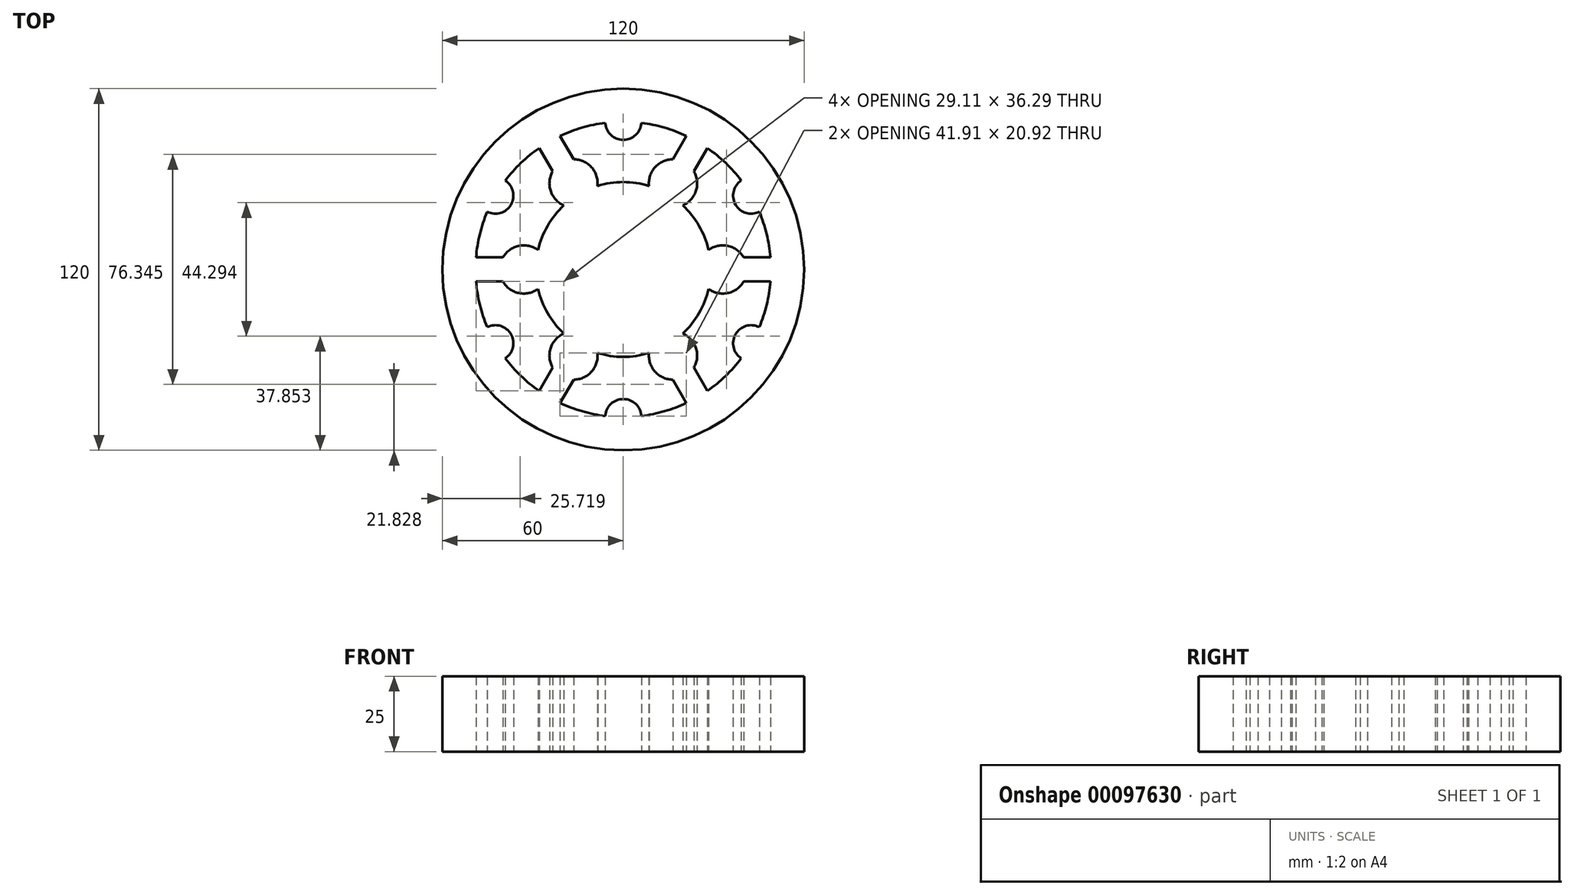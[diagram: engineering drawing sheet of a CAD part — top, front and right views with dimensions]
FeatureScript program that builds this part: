
annotation { "Feature Type Name" : "Feature", "Feature Type Description" : "" }
export const myFeature = defineFeature(function(context is Context, id is Id, definition is map)
    precondition{}
    {
        {
            var Q0;
            Q0=qCreatedBy(makeId("Top.planeOp"),FACE);
            var sketch = newSketch(context, id + "F0", { "sketchPlane" : qUnion([Q0])});
            skArc(sketch, "E0", {"start": v(-45.11, 19.13) * mm, "mid": v(-47.58, 11.71) * mm, "end": v(-48.84, 4) * mm});
            skCircle(sketch, "E1", {"center": v(0, 0) * mm, "radius": 33 * mm, "construction": true});
            skLineSegment(sketch, "E2", {"start": v(0, 0) * mm, "end": v(-49, 0) * mm, "construction": true});
            skLineSegment(sketch, "E3", {"start": v(0, 0) * mm, "end": v(-24.5, 42.44) * mm, "construction": true});
            skArc(sketch, "E4", {"start": v(-28.27, 6.45) * mm, "mid": v(-34.65, 7.83) * mm, "end": v(-39.93, 4) * mm});
            skArc(sketch, "E5", {"start": v(-23.43, 32.58) * mm, "mid": v(-24.1, 26.1) * mm, "end": v(-19.73, 21.26) * mm});
            skLineSegment(sketch, "E6", {"start": v(0, 0) * mm, "end": v(-42.44, 24.5) * mm, "construction": true});
            skArc(sketch, "E7", {"start": v(-45.11, 19.13) * mm, "mid": v(-37.24, 21.5) * mm, "end": v(-39.12, 29.5) * mm});
            skLineSegment(sketch, "E8", {"start": v(-27.88, 40.3) * mm, "end": v(-23.43, 32.58) * mm});
            skLineSegment(sketch, "E9", {"start": v(-48.84, 4) * mm, "end": v(-39.93, 4) * mm});
            skArc(sketch, "E10", {"start": v(-19.73, 21.26) * mm, "mid": v(-25.11, 14.5) * mm, "end": v(-28.27, 6.45) * mm});
            skArc(sketch, "E11.trimOffspring", {"start": v(-27.88, 40.3) * mm, "mid": v(-33.93, 35.35) * mm, "end": v(-39.12, 29.5) * mm});
            skArc(sketch, "E12.1.0", {"start": v(-39.12, -29.5) * mm, "mid": v(-33.93, -35.35) * mm, "end": v(-27.88, -40.3) * mm});
            skArc(sketch, "E12.1.1", {"start": v(-39.12, -29.5) * mm, "mid": v(-37.24, -21.5) * mm, "end": v(-45.11, -19.13) * mm});
            skArc(sketch, "E12.1.2", {"start": v(-48.84, -4) * mm, "mid": v(-47.58, -11.71) * mm, "end": v(-45.11, -19.13) * mm});
            skLineSegment(sketch, "E12.1.3", {"start": v(-27.88, -40.3) * mm, "end": v(-23.43, -32.58) * mm});
            skArc(sketch, "E12.1.4", {"start": v(-19.73, -21.26) * mm, "mid": v(-24.1, -26.1) * mm, "end": v(-23.43, -32.58) * mm});
            skArc(sketch, "E12.1.5", {"start": v(-28.27, -6.45) * mm, "mid": v(-25.11, -14.5) * mm, "end": v(-19.73, -21.26) * mm});
            skArc(sketch, "E12.1.6", {"start": v(-39.93, -4) * mm, "mid": v(-34.65, -7.83) * mm, "end": v(-28.27, -6.45) * mm});
            skLineSegment(sketch, "E12.1.7", {"start": v(-48.84, -4) * mm, "end": v(-39.93, -4) * mm});
            skArc(sketch, "E12.2.0", {"start": v(5.99, -48.63) * mm, "mid": v(13.65, -47.06) * mm, "end": v(20.95, -44.3) * mm});
            skArc(sketch, "E12.2.1", {"start": v(5.99, -48.63) * mm, "mid": v(0, -43) * mm, "end": v(-5.99, -48.63) * mm});
            skArc(sketch, "E12.2.2", {"start": v(-20.95, -44.3) * mm, "mid": v(-13.65, -47.06) * mm, "end": v(-5.99, -48.63) * mm});
            skLineSegment(sketch, "E12.2.3", {"start": v(20.95, -44.3) * mm, "end": v(16.5, -36.58) * mm});
            skArc(sketch, "E12.2.4", {"start": v(8.55, -27.71) * mm, "mid": v(10.54, -33.92) * mm, "end": v(16.5, -36.58) * mm});
            skArc(sketch, "E12.2.5", {"start": v(-8.55, -27.71) * mm, "mid": v(0, -29) * mm, "end": v(8.55, -27.71) * mm});
            skArc(sketch, "E12.2.6", {"start": v(-16.5, -36.58) * mm, "mid": v(-10.54, -33.92) * mm, "end": v(-8.55, -27.71) * mm});
            skLineSegment(sketch, "E12.2.7", {"start": v(-20.95, -44.3) * mm, "end": v(-16.5, -36.58) * mm});
            skArc(sketch, "E12.3.0", {"start": v(45.11, -19.13) * mm, "mid": v(47.58, -11.71) * mm, "end": v(48.84, -4) * mm});
            skArc(sketch, "E12.3.1", {"start": v(45.11, -19.13) * mm, "mid": v(37.24, -21.5) * mm, "end": v(39.12, -29.5) * mm});
            skArc(sketch, "E12.3.2", {"start": v(27.88, -40.3) * mm, "mid": v(33.93, -35.35) * mm, "end": v(39.12, -29.5) * mm});
            skLineSegment(sketch, "E12.3.3", {"start": v(48.84, -4) * mm, "end": v(39.93, -4) * mm});
            skArc(sketch, "E12.3.4", {"start": v(28.27, -6.45) * mm, "mid": v(34.65, -7.83) * mm, "end": v(39.93, -4) * mm});
            skArc(sketch, "E12.3.5", {"start": v(19.73, -21.26) * mm, "mid": v(25.11, -14.5) * mm, "end": v(28.27, -6.45) * mm});
            skArc(sketch, "E12.3.6", {"start": v(23.43, -32.58) * mm, "mid": v(24.1, -26.1) * mm, "end": v(19.73, -21.26) * mm});
            skLineSegment(sketch, "E12.3.7", {"start": v(27.88, -40.3) * mm, "end": v(23.43, -32.58) * mm});
            skArc(sketch, "E12.4.0", {"start": v(39.12, 29.5) * mm, "mid": v(33.93, 35.35) * mm, "end": v(27.88, 40.3) * mm});
            skArc(sketch, "E12.4.1", {"start": v(39.12, 29.5) * mm, "mid": v(37.24, 21.5) * mm, "end": v(45.11, 19.13) * mm});
            skArc(sketch, "E12.4.2", {"start": v(48.84, 4) * mm, "mid": v(47.58, 11.71) * mm, "end": v(45.11, 19.13) * mm});
            skLineSegment(sketch, "E12.4.3", {"start": v(27.88, 40.3) * mm, "end": v(23.43, 32.58) * mm});
            skArc(sketch, "E12.4.4", {"start": v(19.73, 21.26) * mm, "mid": v(24.1, 26.1) * mm, "end": v(23.43, 32.58) * mm});
            skArc(sketch, "E12.4.5", {"start": v(28.27, 6.45) * mm, "mid": v(25.11, 14.5) * mm, "end": v(19.73, 21.26) * mm});
            skArc(sketch, "E12.4.6", {"start": v(39.93, 4) * mm, "mid": v(34.65, 7.83) * mm, "end": v(28.27, 6.45) * mm});
            skLineSegment(sketch, "E12.4.7", {"start": v(48.84, 4) * mm, "end": v(39.93, 4) * mm});
            skArc(sketch, "E12.5.0", {"start": v(-5.99, 48.63) * mm, "mid": v(-13.65, 47.06) * mm, "end": v(-20.95, 44.3) * mm});
            skArc(sketch, "E12.5.1", {"start": v(-5.99, 48.63) * mm, "mid": v(0, 43) * mm, "end": v(5.99, 48.63) * mm});
            skArc(sketch, "E12.5.2", {"start": v(20.95, 44.3) * mm, "mid": v(13.65, 47.06) * mm, "end": v(5.99, 48.63) * mm});
            skLineSegment(sketch, "E12.5.3", {"start": v(-20.95, 44.3) * mm, "end": v(-16.5, 36.58) * mm});
            skArc(sketch, "E12.5.4", {"start": v(-8.55, 27.71) * mm, "mid": v(-10.54, 33.92) * mm, "end": v(-16.5, 36.58) * mm});
            skArc(sketch, "E12.5.5", {"start": v(8.55, 27.71) * mm, "mid": v(0, 29) * mm, "end": v(-8.55, 27.71) * mm});
            skArc(sketch, "E12.5.6", {"start": v(16.5, 36.58) * mm, "mid": v(10.54, 33.92) * mm, "end": v(8.55, 27.71) * mm});
            skLineSegment(sketch, "E12.5.7", {"start": v(20.95, 44.3) * mm, "end": v(16.5, 36.58) * mm});
            skCircle(sketch, "E13", {"center": v(0, 0) * mm, "radius": 60 * mm});
            skSolve(sketch);
        }
        {
            var Q0;
            Q0=makeQuery(id+"F0.imprint","IMPRINT",FACE,{"disambiguationData":[TD([[makeQuery(id+"F0.imprint","IMPRINT",EDGE,{"derivedFrom":sQuery(id+"F0.wireOp",EDGE,"E0")}),-1.0]])]});
            extrude(context, id + "F1", {"entities" : qUnion([Q0]), "depth" : 25 * mm});
        }
    });
